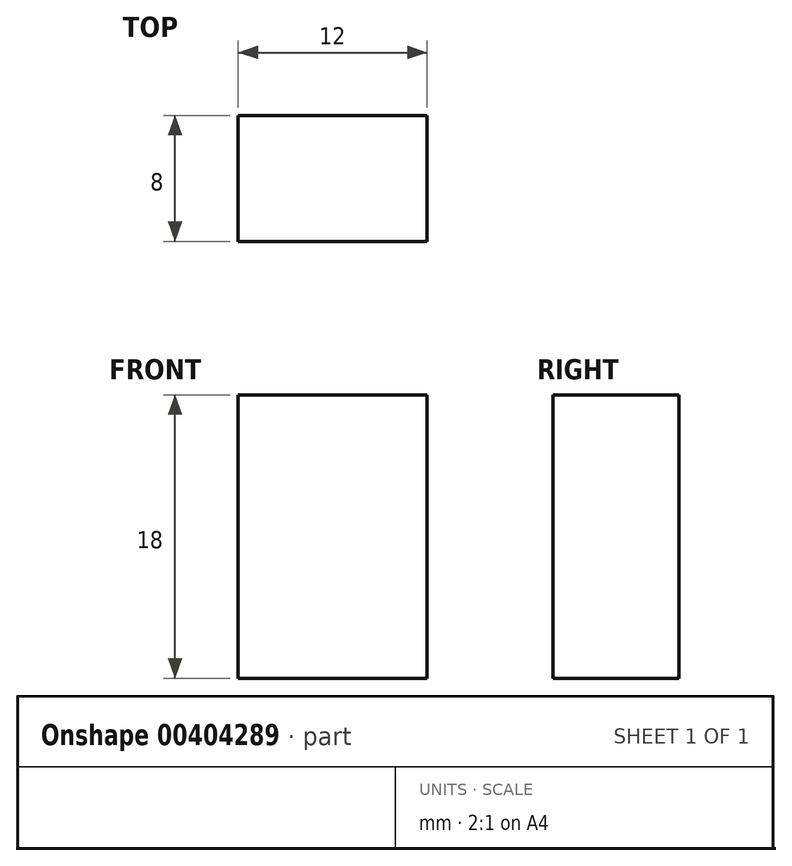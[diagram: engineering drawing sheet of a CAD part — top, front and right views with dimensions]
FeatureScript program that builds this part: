
annotation { "Feature Type Name" : "Feature", "Feature Type Description" : "" }
export const myFeature = defineFeature(function(context is Context, id is Id, definition is map)
    precondition{}
    {
        {
            var Q0;
            Q0=qCreatedBy(makeId("Front.planeOp"),FACE);
            var sketch = newSketch(context, id + "F0", { "sketchPlane" : qUnion([Q0])});
            skLineSegment(sketch, "E0.bottom", {"start": v(0, 0) * mm, "end": v(12, 0) * mm});
            skLineSegment(sketch, "E0.top", {"start": v(0, 18) * mm, "end": v(12, 18) * mm});
            skLineSegment(sketch, "E0.left", {"start": v(0, 0) * mm, "end": v(0, 18) * mm});
            skLineSegment(sketch, "E0.right", {"start": v(12, 0) * mm, "end": v(12, 18) * mm});
            skSolve(sketch);
        }
        {
            var Q0;
            Q0=makeQuery(id+"F0.imprint","IMPRINT",FACE,{"disambiguationData":[TD([[makeQuery(id+"F0.imprint","IMPRINT",EDGE,{"derivedFrom":sQuery(id+"F0.wireOp",EDGE,"E0.bottom")}),1.0]])]});
            extrude(context, id + "F1", {"entities" : qUnion([Q0]), "oppositeDirection" : true, "depth" : 8 * mm});
        }
        {
            var Q0;
            Q0=makeQuery(id+"F1.opExtrude","SWEPT_FACE",FACE,{"disambiguationData":[OSD([sQuery(id+"F0.wireOp",EDGE,"E0.left")])]});
            var sketch = newSketch(context, id + "F2", { "sketchPlane" : qUnion([Q0])});
            skLineSegment(sketch, "E1", {"start": v(0, 18) * mm, "end": v(-8, 0) * mm});
            skLineSegment(sketch, "E2", {"start": v(-8.04, 12.03) * mm, "end": v(0, 6) * mm});
            skPoint(sketch, "E3.orphan", {"position": v(-4, 9) * mm});
            skSolve(sketch);
        }
        {
            var Q0;
            Q0=makeQuery(id+"F1.opExtrude","CAP_FACE",FACE,{"disambiguationData":[OSD([sQuery(id+"F0.wireOp",EDGE,"E0.bottom"),sQuery(id+"F0.wireOp",EDGE,"E0.top"),sQuery(id+"F0.wireOp",EDGE,"E0.left"),sQuery(id+"F0.wireOp",EDGE,"E0.right")])],"isStart":true});
            var sketch = newSketch(context, id + "F3", { "sketchPlane" : qUnion([Q0])});
            skLineSegment(sketch, "E4", {"start": v(0, 18) * mm, "end": v(12, 0) * mm});
            skSolve(sketch);
        }
        {
            var Q0;
            Q0=makeQuery(id+"F1.opExtrude","SWEPT_FACE",FACE,{"disambiguationData":[OSD([sQuery(id+"F0.wireOp",EDGE,"E0.bottom")])]});
            var sketch = newSketch(context, id + "F4", { "sketchPlane" : qUnion([Q0])});
            skLineSegment(sketch, "E5", {"start": v(0, 0) * mm, "end": v(4, -8) * mm});
            skLineSegment(sketch, "E6", {"start": v(12, 0) * mm, "end": v(4, -8) * mm});
            skSolve(sketch);
        }
        {
            var Q0;
            Q0=sQuery(id+"F2.wireOp",EDGE,"E1");
            cPoint(context, id + "F5", {"entities" : qUnion([Q0]), "parameter" : 0.5});
        }
        {
            var Q0;
            Q0=sQuery(id+"F4.wireOp",VERTEX,"E6.end");
            var Q1;
            Q1 = qCreatedBy(id + "F5" ,VERTEX);
            var Q2;
            Q2=sQuery(id+"F2.wireOp",VERTEX,"E2.end");
            cPlane(context, id + "F6", {"entities" : qUnion([Q0, Q1, Q2]), "cplaneType" : CPlaneType.THREE_POINT, "offset" : 25 * mm, "width" : 150 * mm, "height" : 150 * mm});
        }
        {
            var Q0;
            Q0=qCreatedBy(id+"F6.planeOp",FACE);
            var sketch = newSketch(context, id + "F7", { "sketchPlane" : qUnion([Q0])});
            skLineSegment(sketch, "E7", {"start": v(-8.67, -1.25) * mm, "end": v(-4.54, 8.55) * mm});
            skLineSegment(sketch, "E8", {"start": v(-0.43, 5.7) * mm, "end": v(-8.67, -1.25) * mm});
            skSolve(sketch);
        }
        {
            var Q0;
            Q0=sQuery(id+"F2.wireOp",EDGE,"E1");
            cPoint(context, id + "F8", {"entities" : qUnion([Q0]), "parameter" : 0.5});
        }
        {
            var Q0;
            Q0=sQuery(id+"F3.wireOp",VERTEX,"E4.start");
            var Q1;
            Q1 = qCreatedBy(id + "F8" ,VERTEX);
            var Q2;
            Q2=sQuery(id+"F7.wireOp",VERTEX,"E7.start");
            cPlane(context, id + "F9", {"entities" : qUnion([Q0, Q1, Q2]), "cplaneType" : CPlaneType.THREE_POINT, "offset" : 25 * mm, "width" : 150 * mm, "height" : 150 * mm});
        }
        {
            var Q0;
            Q0=makeQuery(id+"F3.imprint","IMPRINT",FACE,{"disambiguationData":[TD([[makeQuery(id+"F3.imprint","IMPRINT",EDGE,{"derivedFrom":sQuery(id+"F3.wireOp",EDGE,"E4")}),-1.0]])]});
            var sketch = newSketch(context, id + "F10", { "sketchPlane" : qUnion([Q0])});
            skLineSegment(sketch, "E9", {"start": v(0, 5.97) * mm, "end": v(12, 4.02) * mm});
            skSolve(sketch);
        }
        {
            var Q0;
            Q0=sQuery(id+"F2.wireOp",EDGE,"E1");
            cPoint(context, id + "F11", {"entities" : qUnion([Q0]), "parameter" : 0.5});
        }
        {
            var Q0;
            Q0=sQuery(id+"F10.wireOp",VERTEX,"E9.end");
            var Q1;
            Q1=sQuery(id+"F2.wireOp",VERTEX,"E2.end");
            var Q2;
            Q2 = qCreatedBy(id + "F11" ,VERTEX);
            cPlane(context, id + "F12", {"entities" : qUnion([Q0, Q1, Q2]), "cplaneType" : CPlaneType.THREE_POINT, "offset" : 25 * mm, "width" : 150 * mm, "height" : 150 * mm});
        }
        {
            var Q0;
            Q0=makeQuery(id+"F3.imprint","IMPRINT",FACE,{"disambiguationData":[TD([[makeQuery(id+"F3.imprint","IMPRINT",EDGE,{"derivedFrom":sQuery(id+"F3.wireOp",EDGE,"E4")}),-1.0]])]});
            cPlane(context, id + "F13", {"entities" : qUnion([Q0]), "cplaneType" : CPlaneType.OFFSET, "offset" : 8 * mm, "oppositeDirection" : true, "width" : 150 * mm, "height" : 150 * mm});
        }
    });
